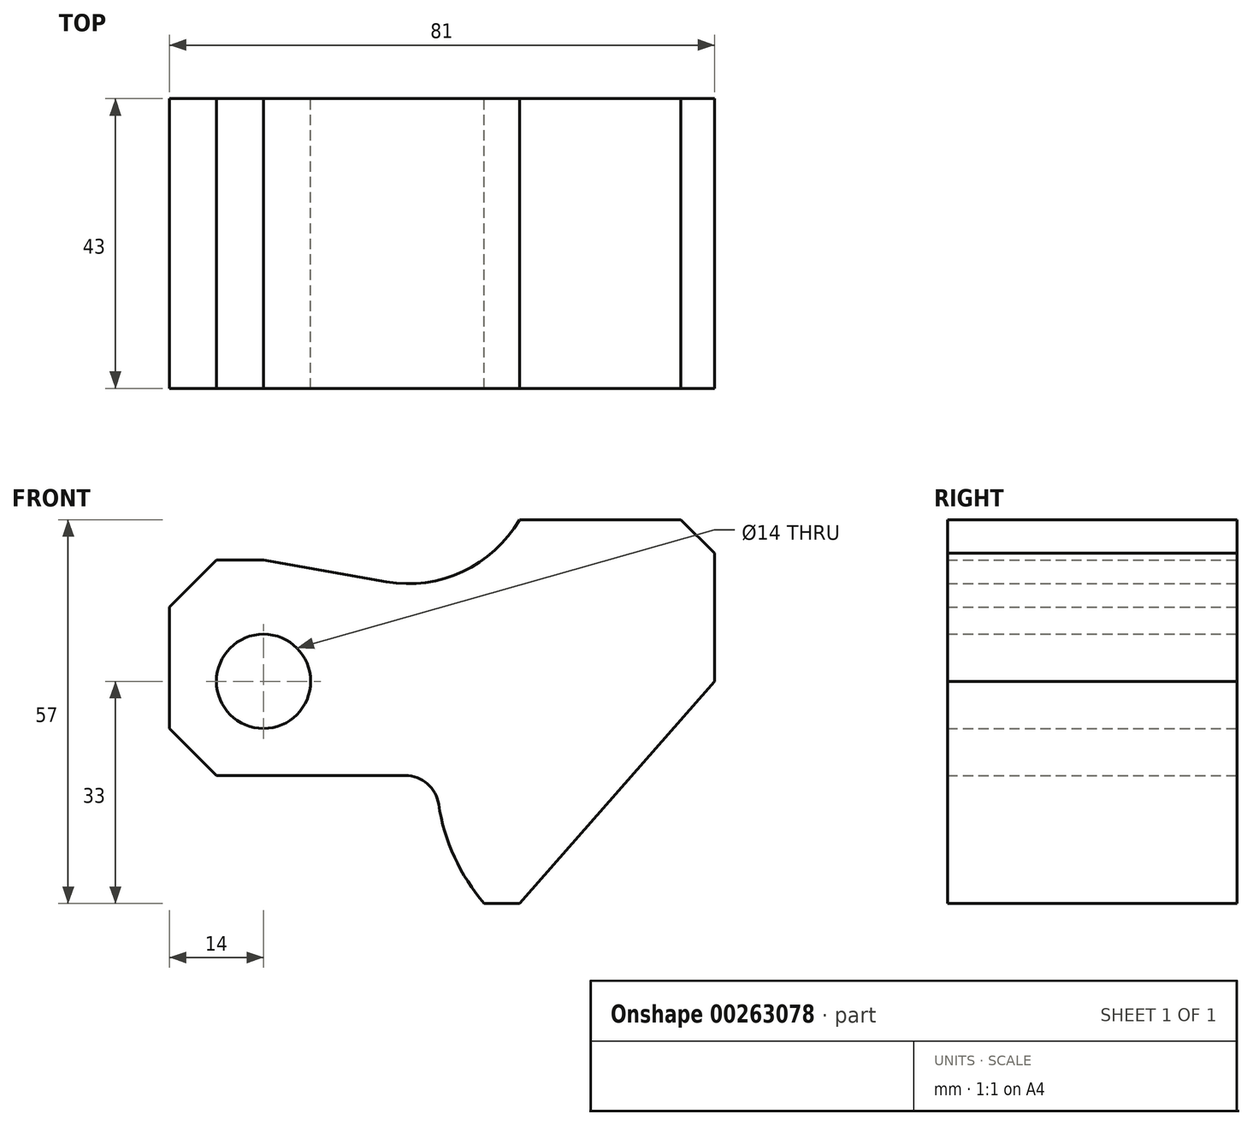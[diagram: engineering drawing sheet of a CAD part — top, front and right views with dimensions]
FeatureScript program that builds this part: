
annotation { "Feature Type Name" : "Feature", "Feature Type Description" : "" }
export const myFeature = defineFeature(function(context is Context, id is Id, definition is map)
    precondition{}
    {
        {
            var Q0;
            Q0=qCreatedBy(makeId("Front.planeOp"),FACE);
            var sketch = newSketch(context, id + "F0", { "sketchPlane" : qUnion([Q0])});
            skCircle(sketch, "E0", {"center": v(0, 0) * mm, "radius": 7 * mm});
            skLineSegment(sketch, "E1", {"start": v(-14, -7) * mm, "end": v(-14, 11) * mm});
            skLineSegment(sketch, "E2", {"start": v(-14, 11) * mm, "end": v(-7, 18) * mm});
            skLineSegment(sketch, "E3", {"start": v(-7, 18) * mm, "end": v(0, 18) * mm});
            skLineSegment(sketch, "E4", {"start": v(0, 18) * mm, "end": v(18.24, 14.78) * mm});
            skArc(sketch, "E5", {"start": v(18.24, 14.78) * mm, "mid": v(29.57, 16.28) * mm, "end": v(38, 24) * mm});
            skLineSegment(sketch, "E6", {"start": v(-14, -7) * mm, "end": v(-7, -14) * mm});
            skLineSegment(sketch, "E7", {"start": v(-7, -14) * mm, "end": v(21.07, -14) * mm});
            skArc(sketch, "E8", {"start": v(21.07, -14) * mm, "mid": v(24.33, -15.21) * mm, "end": v(26.01, -18.26) * mm});
            skArc(sketch, "E9", {"start": v(26.01, -18.26) * mm, "mid": v(28.35, -26.12) * mm, "end": v(32.79, -33) * mm});
            skLineSegment(sketch, "E10", {"start": v(32.79, -33) * mm, "end": v(38, -33) * mm});
            skLineSegment(sketch, "E11", {"start": v(38, -33) * mm, "end": v(67, 0) * mm});
            skLineSegment(sketch, "E12", {"start": v(67, 0) * mm, "end": v(67, 19) * mm});
            skLineSegment(sketch, "E13", {"start": v(67, 19) * mm, "end": v(62, 24) * mm});
            skLineSegment(sketch, "E14", {"start": v(62, 24) * mm, "end": v(38, 24) * mm});
            skSolve(sketch);
        }
        {
            var Q0;
            Q0=makeQuery(id+"F0.imprint","IMPRINT",FACE,{"disambiguationData":[TD([[makeQuery(id+"F0.imprint","IMPRINT",EDGE,{"derivedFrom":sQuery(id+"F0.wireOp",EDGE,"E0")}),-1.0]])]});
            extrude(context, id + "F1", {"entities" : qUnion([Q0]), "depth" : 43 * mm});
        }
    });
